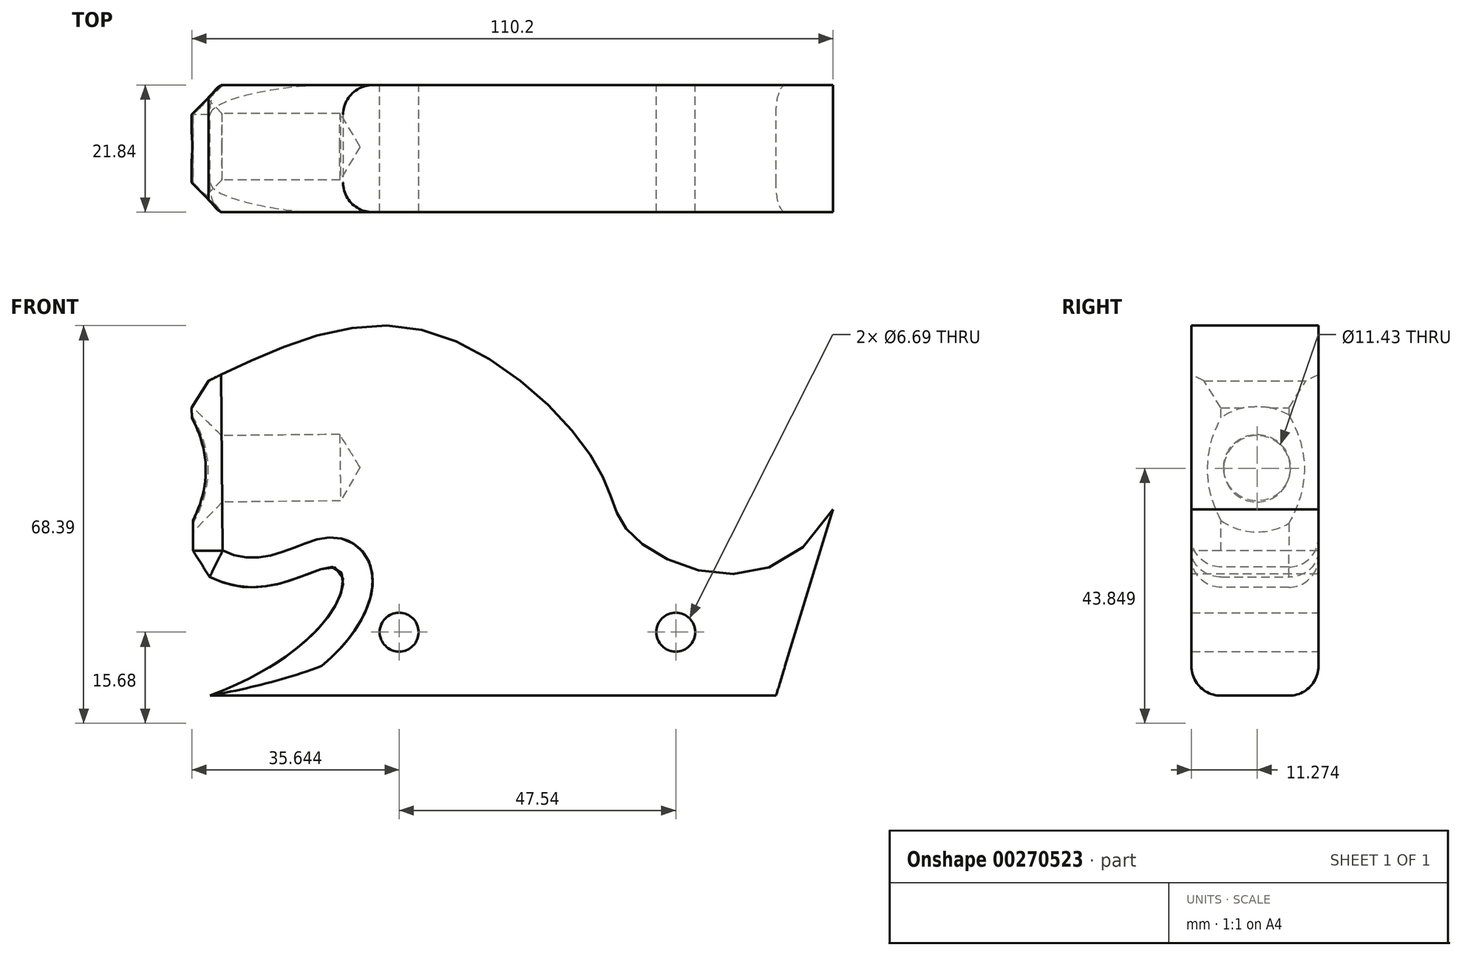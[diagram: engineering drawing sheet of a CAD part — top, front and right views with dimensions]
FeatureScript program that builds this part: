
annotation { "Feature Type Name" : "Feature", "Feature Type Description" : "" }
export const myFeature = defineFeature(function(context is Context, id is Id, definition is map)
    precondition{}
    {
        {
            var Q0;
            Q0=qCreatedBy(makeId("Front.planeOp"),FACE);
            var sketch = newSketch(context, id + "F0", { "sketchPlane" : qUnion([Q0])});
            skLineSegment(sketch, "E0", {"start": v(-74.68, -10.94) * mm, "end": v(22.57, -10.94) * mm});
            skFitSpline(sketch, "E1", {"points": [v(-77.57, 11.15) * mm, v(-53.36, 11.15) * mm, v(-74.68, -10.94) * mm], "startDerivative": vector(72.43, -51.6) * mm, "endDerivative": vector(-126.06, -48.18) * mm});
            skCircle(sketch, "E2", {"center": v(-42.2, 0) * mm, "radius": 3.35 * mm});
            skCircle(sketch, "E3", {"center": v(5.33, 0) * mm, "radius": 3.35 * mm});
            skLineSegment(sketch, "E4", {"start": v(-77.88, 41.83) * mm, "end": v(-77.57, 11.15) * mm});
            skFitSpline(sketch, "E5", {"points": [v(-77.88, 41.83) * mm, v(-39.4, 52.19) * mm, v(-7.75, 27.82) * mm, v(-1.6, 16.12) * mm, v(32.35, 21.1) * mm], "startDerivative": vector(112.18, 52.6) * mm, "endDerivative": vector(110.87, 195.66) * mm});
            skLineSegment(sketch, "E6", {"start": v(32.35, 21.1) * mm, "end": v(22.57, -10.94) * mm});
            skSolve(sketch);
        }
        {
            var Q0;
            Q0=makeQuery(id+"F0.imprint","IMPRINT",FACE,{"disambiguationData":[TD([[makeQuery(id+"F0.imprint","IMPRINT",EDGE,{"derivedFrom":sQuery(id+"F0.wireOp",EDGE,"E0")}),1.0]])]});
            var Q1;
            {var subQ0=sQuery(id+"F0.wireOp",EDGE,"9921bf0b-a1c6-427d-a58f-7b23d5906200");Q1=makeQuery(id+"F0.imprint","IMPRINT",FACE,{"disambiguationData":[TD([[makeQuery(id+"F0.imprint","IMPRINT",EDGE,{"derivedFrom":subQ0}),1.0]])]});}
            extrude(context, id + "F1", {"entities" : qUnion([Q0, Q1]), "depth" : 21.84 * mm});
        }
        {
            var Q0;
            Q0=makeQuery(id+"F1.opExtrude","CAP_EDGE",EDGE,{"disambiguationData":[OSD([sQuery(id+"F0.wireOp",EDGE,"60ec59cb-d5f3-459c-bf67-368aaeac4514")])],"isStart":false});
            var Q1;
            Q1=makeQuery(id+"F1.opExtrude","CAP_EDGE",EDGE,{"disambiguationData":[OSD([sQuery(id+"F0.wireOp",EDGE,"H20aswhx-EBio-9mnv-6lwr-GlBeyGAYvjoM")])],"isStart":false});
            var Q2;
            Q2=makeQuery(id+"F1.opExtrude","CAP_EDGE",EDGE,{"disambiguationData":[OSD([sQuery(id+"F0.wireOp",EDGE,"E1")])],"isStart":false});
            var Q3;
            Q3=makeQuery(id+"F1.opExtrude","CAP_EDGE",EDGE,{"disambiguationData":[OSD([sQuery(id+"F0.wireOp",EDGE,"E0")])],"isStart":false});
            var Q4;
            Q4=makeQuery(id+"F1.opExtrude","CAP_EDGE",EDGE,{"disambiguationData":[OSD([sQuery(id+"F0.wireOp",EDGE,"60ec59cb-d5f3-459c-bf67-368aaeac4514")])],"isStart":true});
            var Q5;
            Q5=makeQuery(id+"F1.opExtrude","CAP_EDGE",EDGE,{"disambiguationData":[OSD([sQuery(id+"F0.wireOp",EDGE,"H20aswhx-EBio-9mnv-6lwr-GlBeyGAYvjoM")])],"isStart":true});
            var Q6;
            Q6=makeQuery(id+"F1.opExtrude","CAP_EDGE",EDGE,{"disambiguationData":[OSD([sQuery(id+"F0.wireOp",EDGE,"E1")])],"isStart":true});
            var Q7;
            Q7=makeQuery(id+"F1.opExtrude","CAP_EDGE",EDGE,{"disambiguationData":[OSD([sQuery(id+"F0.wireOp",EDGE,"E0")])],"isStart":true});
            fillet(context, id + "F2", {"entities" : qUnion([Q0, Q1, Q2, Q3, Q4, Q5, Q6, Q7]), "radius" : 5.08 * mm, "tangentPropagation" : true, "allowEdgeOverflow" : false});
        }
        {
            var Q0;
            Q0=makeQuery(id+"F1.opExtrude","SWEPT_FACE",FACE,{"disambiguationData":[OSD([sQuery(id+"F0.wireOp",EDGE,"E4")])]});
            var sketch = newSketch(context, id + "F3", { "sketchPlane" : qUnion([Q0])});
            skLineSegment(sketch, "E7.bottom", {"start": v(16.59, 22.78) * mm, "end": v(4.55, 22.78) * mm});
            skLineSegment(sketch, "E7.top", {"start": v(16.59, 34.82) * mm, "end": v(4.55, 34.82) * mm});
            skLineSegment(sketch, "E7.left", {"start": v(16.59, 22.78) * mm, "end": v(16.59, 34.82) * mm});
            skLineSegment(sketch, "E7.right", {"start": v(4.55, 22.78) * mm, "end": v(4.55, 34.82) * mm});
            skPoint(sketch, "E7.middle", {"position": v(10.57, 28.8) * mm});
            skSolve(sketch);
        }
        {
            var Q0;
            Q0=sQuery(id+"F3.wireOp",VERTEX,"E7.middle");
            var Q1;
            Q1=makeQuery(id+"F1.opExtrude","SWEPT_BODY",BODY,{"disambiguationData":[OSD([sQuery(id+"F0.wireOp",EDGE,"E0"),sQuery(id+"F0.wireOp",EDGE,"cygKq6P4-SDen-StYQ-JenX-Z4FlfakZFtIx"),sQuery(id+"F0.wireOp",EDGE,"E1"),sQuery(id+"F0.wireOp",EDGE,"E2"),sQuery(id+"F0.wireOp",EDGE,"E3"),sQuery(id+"F0.wireOp",EDGE,"E4"),sQuery(id+"F0.wireOp",EDGE,"bd86ac56-b67a-40cb-8041-fcb0cfbd5bb0")])]});
            hole(context, id + "F4", {"style" : HoleStyle.SIMPLE, "endStyle" : HoleEndStyle.BLIND, "holeDiameter" : 11.43 * mm, "holeDepth" : 25.4 * mm, "tappedDepth" : 12.7 * mm, "tapClearance" : 3, "locations" : qUnion([Q0]), "scope" : qUnion([Q1])});
        }
        {
            var Q0;
            Q0=makeQuery(id+"F1.opExtrude","CAP_EDGE",EDGE,{"disambiguationData":[OSD([sQuery(id+"F0.wireOp",EDGE,"E4")])],"isStart":false});
            var Q1;
            Q1=makeQuery(id+"F1.opExtrude","CAP_EDGE",EDGE,{"disambiguationData":[OSD([sQuery(id+"F0.wireOp",EDGE,"E4")])],"isStart":true});
            var Q2;
            Q2=makeQuery(id+"F1.opExtrude","SWEPT_FACE",FACE,{"disambiguationData":[OSD([sQuery(id+"F0.wireOp",EDGE,"E4")])]});
            chamfer(context, id + "F5", {"entities" : qUnion([Q0, Q1, Q2]), "width" : 5.08 * mm, "tangentPropagation" : true});
        }
    });
